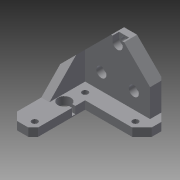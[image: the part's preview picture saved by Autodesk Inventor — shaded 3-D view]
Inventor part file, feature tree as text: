
AUTODESK INVENTOR PART (.ipt)
format: ipt  version: 2015 (Build 190159000, 159)  size: 215,040 bytes
history: native  units: mm
features: sketch x10, extrude x7, chamfer x4, hole x3
ambient origin geometry x8: Origin, YZ Plane, XZ Plane, XY Plane, X Axis, Y Axis, Z Axis, Center Point
bodies: Solid1 (feature_tree)
feature tree (24):
  extrude  "Extrusion1"  Depth=50.0mm
  extrude  "Extrusion2"  Depth=15.0mm
  extrude  "Extrusion3"  Depth=38.0mm TaperAngle=0.0deg
  extrude  "Extrusion4"  Depth=5.0mm
  extrude  "Extrusion5"  TaperAngle=0.0deg  [1 undecoded]
  chamfer  "Chamfer1"  Distance=17.0mm
  chamfer  "Chamfer2"  Distance=33.0mm
  chamfer  "Chamfer3"  [1 undecoded]
  chamfer  "Chamfer4"  Distance=17.0mm
  hole  "Hole1"  [1 undecoded]
  hole  "Hole2"  [1 undecoded]
  hole  "Hole3"  [1 undecoded]
  extrude  "Extrusion6"  TaperAngle=0.0deg  [1 undecoded]
  extrude  "Extrusion7"  Depth=5.0mm TaperAngle=45.0deg
  sketch  "Sketch2"  dims[d0=50.0mm d1=50.0mm]
  sketch  "Sketch3"  dims[d2=38.0mm d3=0.0mm d4=15.0mm]
  sketch  "Sketch4"  dims[d5=18.0mm d6=38.0mm d7=0.0mm]
  sketch  "Sketch6"  dims[d8=8.0mm d9=5.0mm]
  sketch  "Sketch8"  dims[d10=33.0mm d11=0.0mm]
  sketch  "Sketch9"  dims[d12=8.0mm]
  sketch  "Sketch10"  dims[d13=5.0mm]
  sketch  "Sketch11"  dims[d14=5.0mm]
  sketch  "Sketch12"  dims[d15=135.0deg]
  sketch  "Sketch13"  dims[d16=135.0deg d17=17.0mm d18=33.0mm d19=0.0mm d20=17.0mm d21=5.5mm d22=20.0mm d23=33.0mm d24=0.0mm d25=5.0mm d26=5.0mm d27=45.0deg d28=3.0mm d29=3.0mm d30=45.0deg d31=6.0mm d32=6.0mm d33=45.0deg d34=6.0mm d35=6.0mm d36=45.0deg d37=20.0mm d38=10.0mm d39=20.0mm d40=3.0mm d41=3.6mm d42=6.0mm d43=6.2mm d44=4.0mm d45=90.0deg d46=8.0mm d47=20.594885mm d48=4.2mm d49=4.2mm d50=31.0mm d51=31.0mm d52=3.6mm d53=6.0mm d54=4.0mm d55=2.0mm d56=90.0deg d57=8.0mm d58=20.594885mm d59=5.8mm d60=25.0mm d61=8.0mm d62=6.0mm d63=4.0mm d64=2.0mm d65=90.0deg d66=8.0mm d67=20.594885mm d68=25.0mm d69=0.6mm d70=2.0mm d71=10.0mm d72=0.0mm d73=6.2mm d74=4.0mm d75=10.0mm d76=0.0mm]
note: 6 required parameter values undecoded (feature->parameter linkage not recoverable at this tier; creation-order binding heuristic only, values carry confidence <= 0.55)
